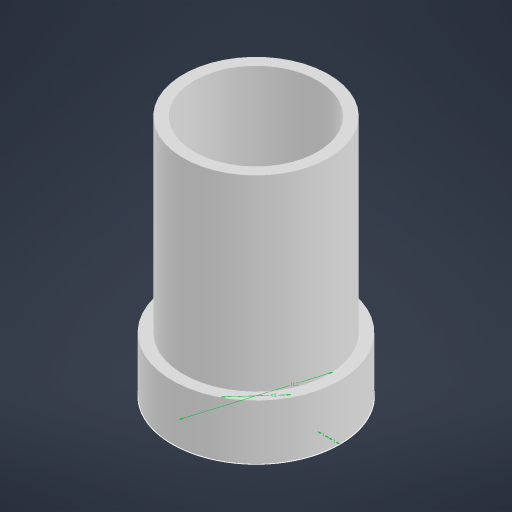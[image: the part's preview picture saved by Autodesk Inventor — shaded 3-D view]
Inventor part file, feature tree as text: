
AUTODESK INVENTOR PART (.ipt)
format: ipt  version: 2024.1 (Build 281209000, 209)  size: 179,200 bytes
history: native  units: mm
features: extrude x3, sketch x2
ambient origin geometry x8: Origin, YZ Plane, XZ Plane, XY Plane, X Axis, Y Axis, Z Axis, Center Point
bodies: Solid1 (feature_tree)
feature tree (5):
  sketch  "Sketch1"  dims[d0=11.2mm d1=4.5mm]
  extrude  "Extrusion1"  Depth=4.5mm
  extrude  "Extrusion3"  Depth=17.0mm
  extrude  "Extrusion5"  Depth=5.0mm TaperAngle=0.0deg
  sketch  "Sketch4"  dims[d6=1.0mm d7=1.0mm d8=5.0mm d9=0.0mm d14=17.0mm d15=0.0mm d19=2.5mm d20=15.0mm d21=0.0mm]
